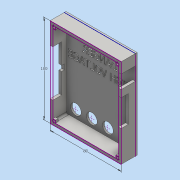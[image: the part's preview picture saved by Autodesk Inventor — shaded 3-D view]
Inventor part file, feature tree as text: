
AUTODESK INVENTOR PART (.ipt)
format: ipt  version: 2016 (Build 200138000, 138)  size: 484,352 bytes
history: native  units: mm
features: extrude x6, sketch x5, hole x2
ambient origin geometry x8: Origin, YZ Plane, XZ Plane, XY Plane, X Axis, Y Axis, Z Axis, Center Point
bodies: Solid1 (feature_tree)
feature tree (13):
  sketch  "Sketch1"  dims[d2=80.0mm d3=100.0mm]
  extrude  "Extrusion1"  Depth=100.0mm
  extrude  "Extrusion2"  Depth=3.0mm TaperAngle=0.0deg
  hole  "Hole1"  [1 undecoded]
  sketch  "Sketch2"  dims[d4=16.0mm d5=0.0mm d6=3.0mm d7=0.0mm]
  extrude  "Extrusion3"  Depth=4.0mm TaperAngle=0.0deg
  hole  "Hole2"  [1 undecoded]
  extrude  "Extrusion4"  Depth=4.0mm
  extrude  "Extrusion5"  Depth=4.0mm
  extrude  "Extrusion6"  Depth=4.0mm TaperAngle=0.0deg
  sketch  "Sketch3"  dims[d8=3.0mm d9=6.0mm d10=4.0mm d11=2.0mm d12=90.0deg d13=8.0mm d14=20.594885mm d15=2.0mm d16=0.0mm]
  sketch  "Sketch4"  dims[d17=12.0mm d18=6.0mm d19=4.0mm d20=2.0mm d21=90.0deg d22=8.0mm d23=20.594885mm d24=4.0mm d25=0.0mm]
  sketch  "Sketch5"  dims[d26=4.0mm d27=0.0mm d31=20.0mm d39=4.0mm d40=4.0mm d41=4.0mm d42=0.0mm]
note: 2 required parameter values undecoded (feature->parameter linkage not recoverable at this tier; creation-order binding heuristic only, values carry confidence <= 0.55)
